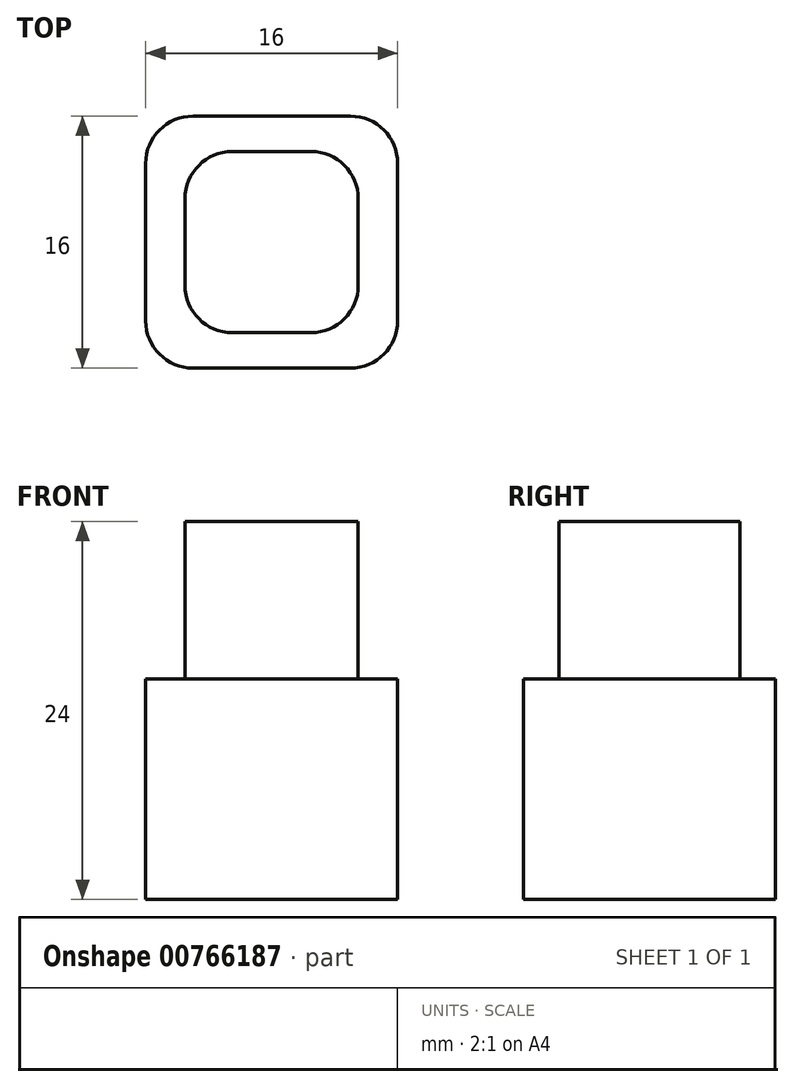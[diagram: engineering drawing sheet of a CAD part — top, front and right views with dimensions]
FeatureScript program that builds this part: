
annotation { "Feature Type Name" : "Feature", "Feature Type Description" : "" }
export const myFeature = defineFeature(function(context is Context, id is Id, definition is map)
    precondition{}
    {
        {
            var Q0;
            Q0=qCreatedBy(makeId("Top.planeOp"),FACE);
            var sketch = newSketch(context, id + "F0", { "sketchPlane" : qUnion([Q0])});
            skLineSegment(sketch, "E0.bottom", {"start": v(-8, 8) * mm, "end": v(8, 8) * mm});
            skLineSegment(sketch, "E0.top", {"start": v(-8, -8) * mm, "end": v(8, -8) * mm});
            skLineSegment(sketch, "E0.left", {"start": v(-8, 8) * mm, "end": v(-8, -8) * mm});
            skLineSegment(sketch, "E0.right", {"start": v(8, 8) * mm, "end": v(8, -8) * mm});
            skPoint(sketch, "E0.middle", {"position": v(0, 0) * mm});
            skSolve(sketch);
        }
        {
            var Q0;
            Q0=makeQuery(id+"F0.imprint","IMPRINT",FACE,{"disambiguationData":[TD([[makeQuery(id+"F0.imprint","IMPRINT",EDGE,{"derivedFrom":sQuery(id+"F0.wireOp",EDGE,"E0.bottom")}),-1.0]])]});
            extrude(context, id + "F1", {"entities" : qUnion([Q0]), "depth" : 14 * mm, "offsetDistance" : 25 * mm});
        }
        {
            var Q0;
            Q0=makeQuery(id+"F1.opExtrude","CAP_FACE",FACE,{"disambiguationData":[OSD([sQuery(id+"F0.wireOp",EDGE,"E0.bottom"),sQuery(id+"F0.wireOp",EDGE,"E0.top"),sQuery(id+"F0.wireOp",EDGE,"E0.left"),sQuery(id+"F0.wireOp",EDGE,"E0.right")])],"isStart":false});
            var sketch = newSketch(context, id + "F2", { "sketchPlane" : qUnion([Q0])});
            skLineSegment(sketch, "E1.bottom", {"start": v(-5.5, 5.75) * mm, "end": v(5.5, 5.75) * mm});
            skLineSegment(sketch, "E1.top", {"start": v(-5.5, -5.75) * mm, "end": v(5.5, -5.75) * mm});
            skLineSegment(sketch, "E1.left", {"start": v(-5.5, 5.75) * mm, "end": v(-5.5, -5.75) * mm});
            skLineSegment(sketch, "E1.right", {"start": v(5.5, 5.75) * mm, "end": v(5.5, -5.75) * mm});
            skPoint(sketch, "E1.middle", {"position": v(0, 0) * mm});
            skSolve(sketch);
        }
        {
            var Q0;
            Q0=makeQuery(id+"F2.imprint","IMPRINT",FACE,{"disambiguationData":[TD([[makeQuery(id+"F2.imprint","IMPRINT",EDGE,{"derivedFrom":sQuery(id+"F2.wireOp",EDGE,"E1.bottom")}),-1.0]])]});
            extrude(context, id + "F3", {"entities" : qUnion([Q0]), "operationType" : NewBodyOperationType.ADD, "depth" : 10 * mm, "offsetDistance" : 25 * mm});
        }
        {
            var Q0;
            Q0=makeQuery(id+"F3.opExtrude","SWEPT_EDGE",EDGE,{"disambiguationData":[OSD([sQuery(id+"F2.wireOp",EDGE,"E1.top"),sQuery(id+"F2.wireOp",EDGE,"E1.right")])]});
            var Q1;
            Q1=makeQuery(id+"F3.opExtrude","SWEPT_EDGE",EDGE,{"disambiguationData":[OSD([sQuery(id+"F2.wireOp",EDGE,"E1.bottom"),sQuery(id+"F2.wireOp",EDGE,"E1.right")])]});
            var Q2;
            Q2=makeQuery(id+"F3.opExtrude","SWEPT_EDGE",EDGE,{"disambiguationData":[OSD([sQuery(id+"F2.wireOp",EDGE,"E1.top"),sQuery(id+"F2.wireOp",EDGE,"E1.left")])]});
            var Q3;
            Q3=makeQuery(id+"F1.opExtrude","SWEPT_EDGE",EDGE,{"disambiguationData":[OSD([sQuery(id+"F0.wireOp",EDGE,"E0.top"),sQuery(id+"F0.wireOp",EDGE,"E0.left")])]});
            var Q4;
            Q4=makeQuery(id+"F1.opExtrude","SWEPT_EDGE",EDGE,{"disambiguationData":[OSD([sQuery(id+"F0.wireOp",EDGE,"E0.top"),sQuery(id+"F0.wireOp",EDGE,"E0.right")])]});
            var Q5;
            Q5=makeQuery(id+"F1.opExtrude","SWEPT_EDGE",EDGE,{"disambiguationData":[OSD([sQuery(id+"F0.wireOp",EDGE,"E0.bottom"),sQuery(id+"F0.wireOp",EDGE,"E0.right")])]});
            var Q6;
            Q6=makeQuery(id+"F1.opExtrude","SWEPT_EDGE",EDGE,{"disambiguationData":[OSD([sQuery(id+"F0.wireOp",EDGE,"E0.bottom"),sQuery(id+"F0.wireOp",EDGE,"E0.left")])]});
            var Q7;
            Q7=makeQuery(id+"F3.opExtrude","SWEPT_EDGE",EDGE,{"disambiguationData":[OSD([sQuery(id+"F2.wireOp",EDGE,"E1.bottom"),sQuery(id+"F2.wireOp",EDGE,"E1.left")])]});
            fillet(context, id + "F4", {"entities" : qUnion([Q0, Q1, Q2, Q3, Q4, Q5, Q6, Q7]), "radius" : 3 * mm, "tangentPropagation" : true, "allowEdgeOverflow" : false});
        }
    });
